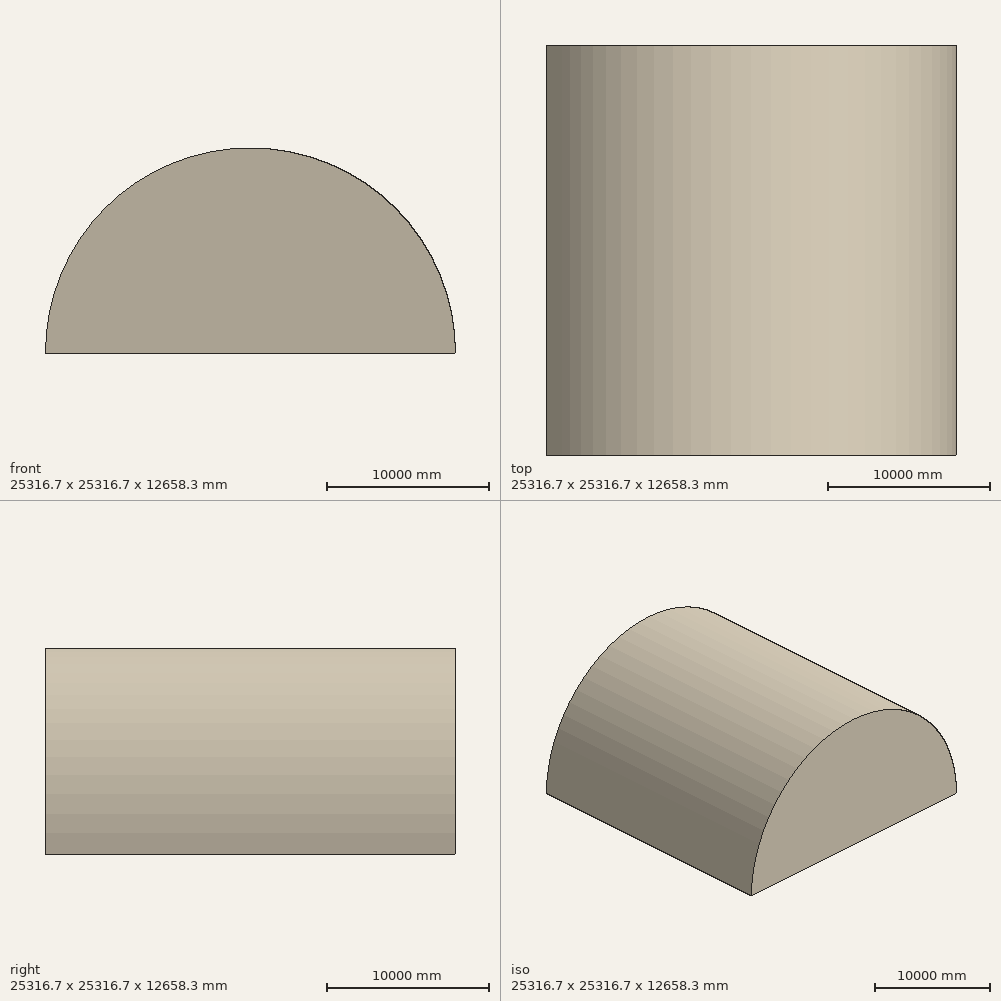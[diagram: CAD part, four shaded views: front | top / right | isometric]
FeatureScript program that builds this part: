
annotation { "Feature Type Name" : "Feature", "Feature Type Description" : "" }
export const myFeature = defineFeature(function(context is Context, id is Id, definition is map)
    precondition{}
    {
        {
            var Q0;
            Q0=qCreatedBy(makeId("Front.planeOp"),FACE);
            var sketch = newSketch(context, id + "F0", { "sketchPlane" : qUnion([Q0])});
            skArc(sketch, "E0", {"start": v(12658.34, 0) * mm, "mid": v(0, 12658.34) * mm, "end": v(-12658.34, 0) * mm});
            skLineSegment(sketch, "E1", {"start": v(0, 0) * mm, "end": v(12658.34, 0) * mm});
            skLineSegment(sketch, "E2", {"start": v(0, 0) * mm, "end": v(-12658.34, 0) * mm});
            skSolve(sketch);
        }
        {
            var Q0;
            {var subQ0=sQuery(id+"F0.wireOp",EDGE,"E1");Q0=makeQuery(id+"F0.imprint","IMPRINT",FACE,{"disambiguationData":[TD([[makeQuery(id+"F0.imprint","IMPRINT",EDGE,{"derivedFrom":subQ0}),1.0]])]});}
            extrude(context, id + "F1", {"entities" : qUnion([Q0]), "depth" : 25316.69 * mm, "offsetDistance" : 25.4 * mm});
        }
    });
